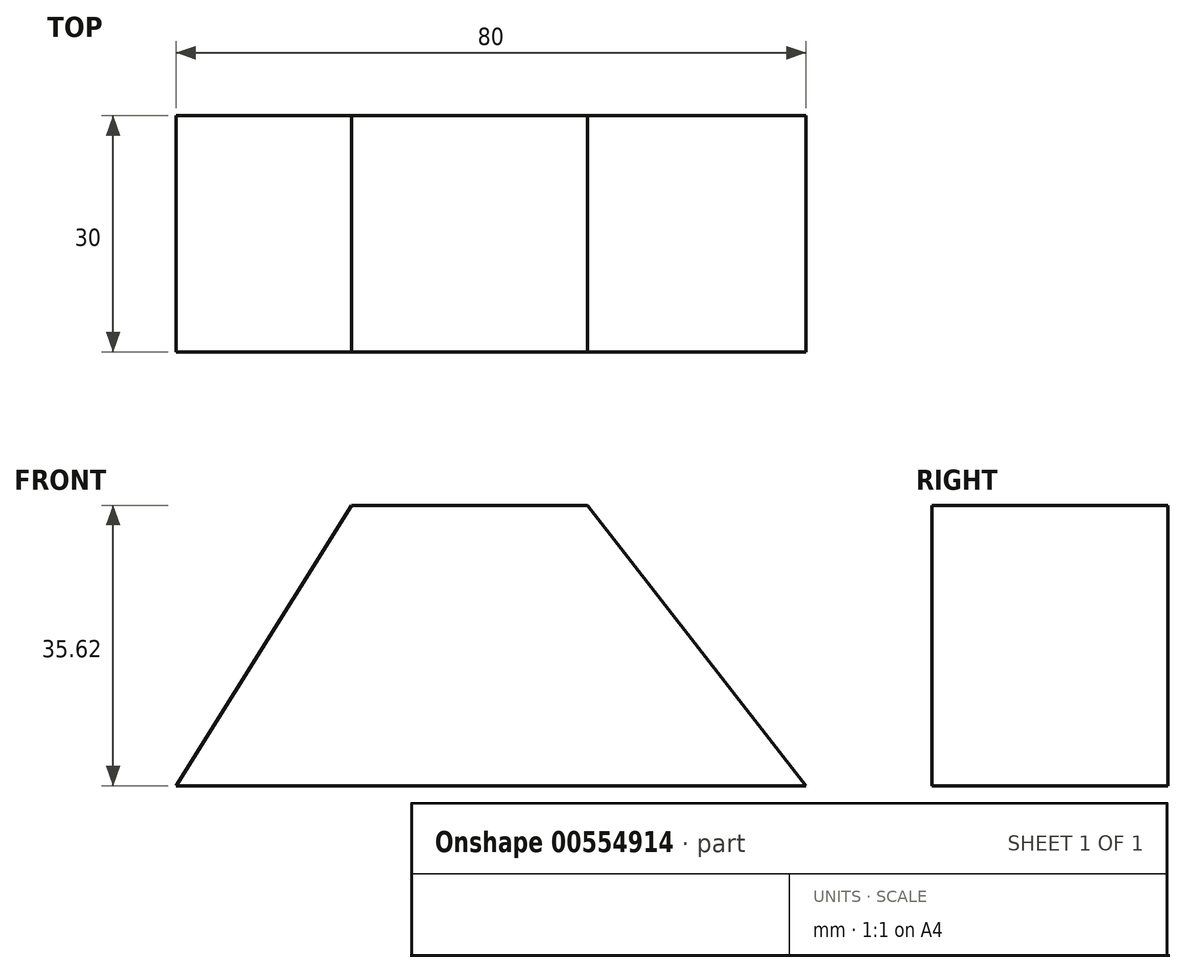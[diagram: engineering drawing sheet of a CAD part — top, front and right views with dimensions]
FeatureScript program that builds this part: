
annotation { "Feature Type Name" : "Feature", "Feature Type Description" : "" }
export const myFeature = defineFeature(function(context is Context, id is Id, definition is map)
    precondition{}
    {
        {
            var Q0;
            Q0=qCreatedBy(makeId("Front.planeOp"),FACE);
            var sketch = newSketch(context, id + "F0", { "sketchPlane" : qUnion([Q0])});
            skLineSegment(sketch, "E0", {"start": v(-52.26, -27.38) * mm, "end": v(27.74, -27.38) * mm});
            skLineSegment(sketch, "E1", {"start": v(27.74, -27.38) * mm, "end": v(0, 8.24) * mm});
            skLineSegment(sketch, "E2", {"start": v(0, 8.24) * mm, "end": v(-30, 8.24) * mm});
            skLineSegment(sketch, "E3", {"start": v(-30, 8.24) * mm, "end": v(-52.26, -27.38) * mm});
            skSolve(sketch);
        }
        {
            var Q0;
            Q0 = qSketchRegion(id + "F0", true);
            extrude(context, id + "F1", {"entities" : qUnion([Q0]), "depth" : 30 * mm, "offsetDistance" : 25 * mm});
        }
    });
